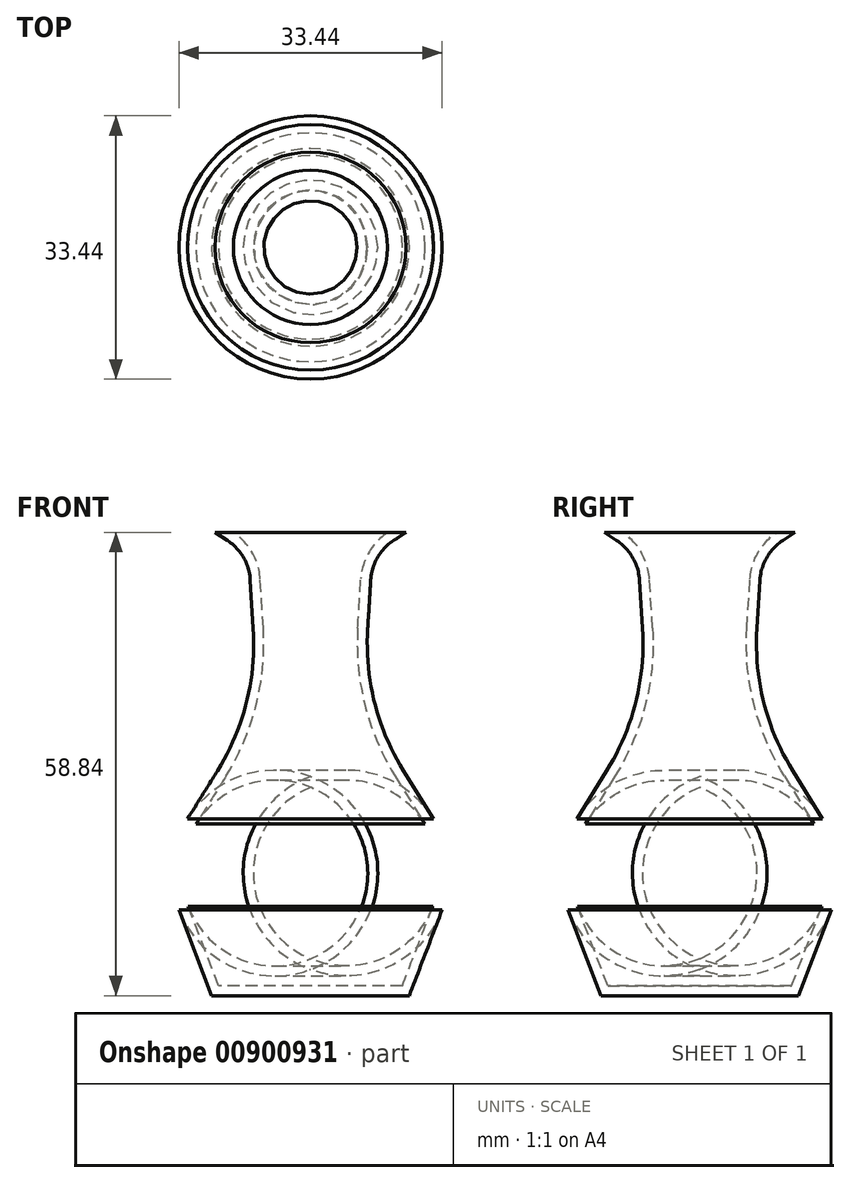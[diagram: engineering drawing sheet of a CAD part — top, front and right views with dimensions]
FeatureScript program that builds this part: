
annotation { "Feature Type Name" : "Feature", "Feature Type Description" : "" }
export const myFeature = defineFeature(function(context is Context, id is Id, definition is map)
    precondition{}
    {
        {
            var Q0;
            Q0=qCreatedBy(makeId("Front.planeOp"),FACE);
            var sketch = newSketch(context, id + "F0", { "sketchPlane" : qUnion([Q0])});
            skLineSegment(sketch, "E0", {"start": v(0, 0) * mm, "end": v(12.55, 0) * mm});
            skLineSegment(sketch, "E1", {"start": v(12.55, 0) * mm, "end": v(19.04, 16.97) * mm});
            skLineSegment(sketch, "E2", {"start": v(19.04, 16.97) * mm, "end": v(6.65, 36.87) * mm});
            skLineSegment(sketch, "E3", {"start": v(6.65, 36.87) * mm, "end": v(7.86, 56.05) * mm});
            skLineSegment(sketch, "E4", {"start": v(7.86, 56.05) * mm, "end": v(12.11, 58.84) * mm});
            skLineSegment(sketch, "E5", {"start": v(12.11, 58.84) * mm, "end": v(0, 58.84) * mm});
            skLineSegment(sketch, "E6", {"start": v(0, 58.84) * mm, "end": v(0, 0) * mm});
            skLineSegment(sketch, "E7", {"start": v(0, 58.84) * mm, "end": v(0, 74.52) * mm});
            skSolve(sketch);
        }
        {
            var Q0;
            Q0=makeQuery(id+"F0.imprint","IMPRINT",FACE,{"disambiguationData":[TD([[makeQuery(id+"F0.imprint","IMPRINT",EDGE,{"derivedFrom":sQuery(id+"F0.wireOp",EDGE,"E0")}),1.0]])]});
            var Q1;
            Q1=sQuery(id+"F0.wireOp",EDGE,"E6");
            revolve(context, id + "F1", {"surfaceOperationType" : NewSurfaceOperationType.NEW, "entities" : qUnion([Q0]), "axis" : qUnion([Q1]), "revolveType" : RevolveType.FULL});
        }
        {
            var Q0;
            Q0=makeQuery(id+"F1.opRevolve","SWEPT_EDGE",EDGE,{"disambiguationData":[OSD([sQuery(id+"F0.wireOp",EDGE,"E1"),sQuery(id+"F0.wireOp",EDGE,"E2")])]});
            fillet(context, id + "F2", {"entities" : qUnion([Q0]), "radius" : 13.07 * mm, "tangentPropagation" : true, "allowEdgeOverflow" : false});
        }
        {
            var Q0;
            Q0=makeQuery(id+"F1.opRevolve","SWEPT_EDGE",EDGE,{"disambiguationData":[OSD([sQuery(id+"F0.wireOp",EDGE,"E2"),sQuery(id+"F0.wireOp",EDGE,"E3")])]});
            fillet(context, id + "F3", {"entities" : qUnion([Q0]), "radius" : 30.53 * mm, "tangentPropagation" : true, "allowEdgeOverflow" : false});
        }
        {
            var Q0;
            Q0=makeQuery(id+"F1.opRevolve","SWEPT_EDGE",EDGE,{"disambiguationData":[OSD([sQuery(id+"F0.wireOp",EDGE,"E3"),sQuery(id+"F0.wireOp",EDGE,"E4")])]});
            fillet(context, id + "F4", {"entities" : qUnion([Q0]), "radius" : 6.45 * mm, "tangentPropagation" : true, "allowEdgeOverflow" : false});
        }
        {
            var Q0;
            Q0=makeQuery(id+"F1.opRevolve","SWEPT_FACE",FACE,{"disambiguationData":[OSD([sQuery(id+"F0.wireOp",EDGE,"E5")])]});
            shell(context, id + "F5", {"entities" : qUnion([Q0]), "thickness" : 1.27 * mm});
        }
    });
